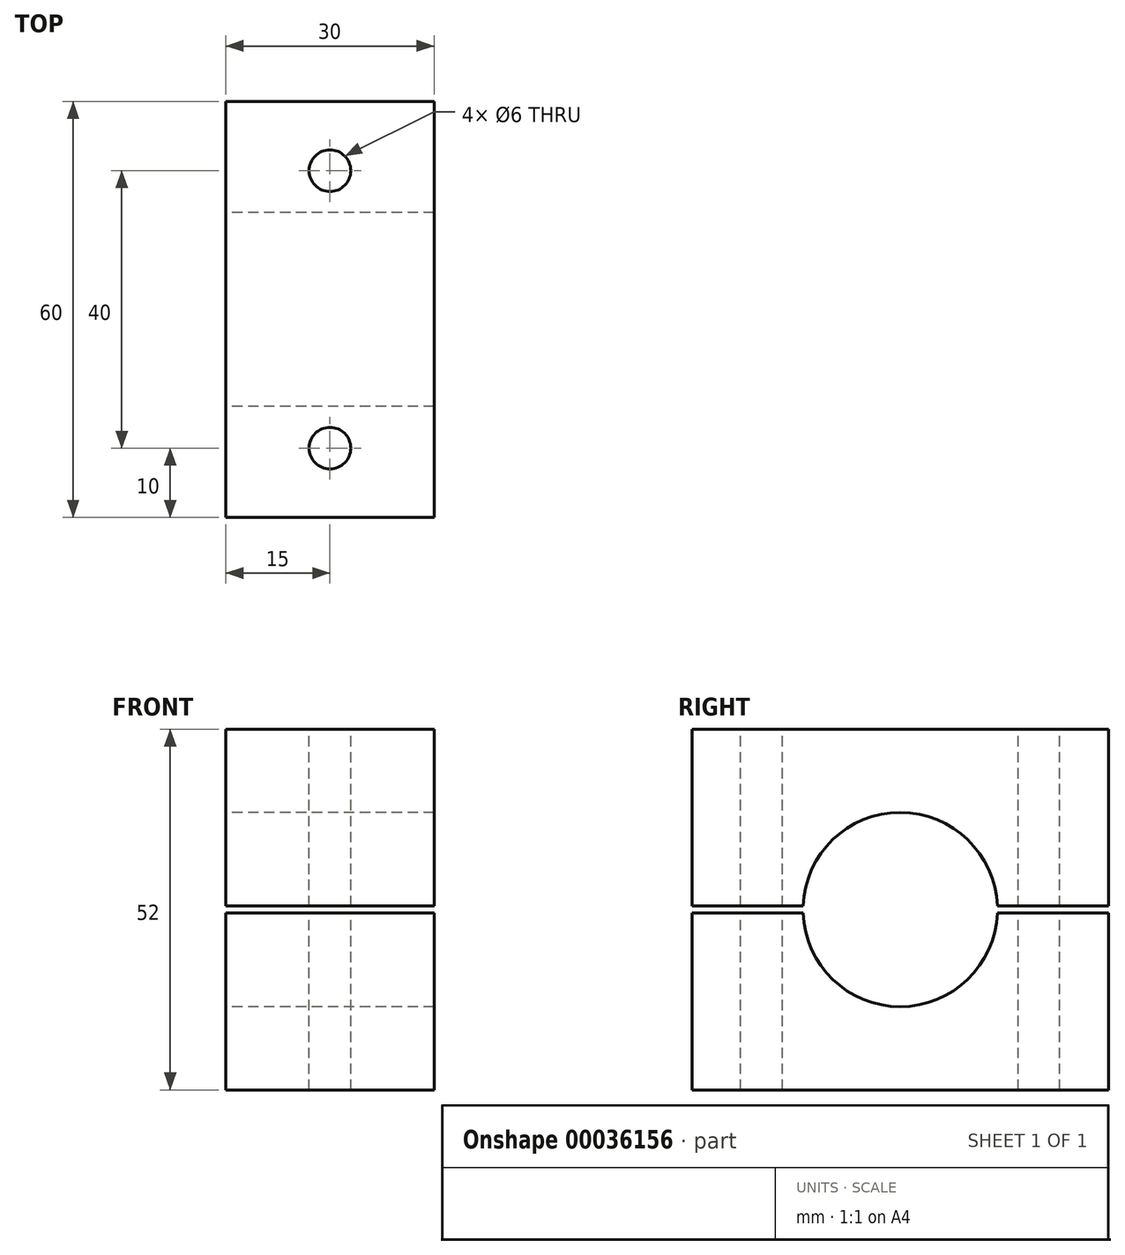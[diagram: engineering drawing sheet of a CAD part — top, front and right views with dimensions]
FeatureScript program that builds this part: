
annotation { "Feature Type Name" : "Feature", "Feature Type Description" : "" }
export const myFeature = defineFeature(function(context is Context, id is Id, definition is map)
    precondition{}
    {
        {
            var Q0;
            Q0=qCreatedBy(makeId("Right.planeOp"),FACE);
            var sketch = newSketch(context, id + "F0", { "sketchPlane" : qUnion([Q0])});
            skLineSegment(sketch, "E0.rect.bottom", {"start": v(30, -26) * mm, "end": v(-30, -26) * mm});
            skLineSegment(sketch, "E0.rect.top", {"start": v(30, 26) * mm, "end": v(-30, 26) * mm});
            skPoint(sketch, "E0.rect.middle", {"position": v(0, 0) * mm});
            skArc(sketch, "E1", {"start": v(-14, -0.5) * mm, "mid": v(0, -14) * mm, "end": v(14, -0.5) * mm});
            skLineSegment(sketch, "E2", {"start": v(-30, 26) * mm, "end": v(-30, 0.5) * mm});
            skLineSegment(sketch, "E3", {"start": v(30, -26) * mm, "end": v(30, -0.5) * mm});
            skLineSegment(sketch, "E4.0", {"start": v(-30, -0.5) * mm, "end": v(-14, -0.5) * mm});
            skLineSegment(sketch, "E5.0", {"start": v(-30, 0.5) * mm, "end": v(-14, 0.5) * mm});
            skLineSegment(sketch, "E6.trimOffspring", {"start": v(14, -0.5) * mm, "end": v(30, -0.5) * mm});
            skLineSegment(sketch, "E7.trimOffspring", {"start": v(14, 0.5) * mm, "end": v(30, 0.5) * mm});
            skLineSegment(sketch, "E8.trimOffspring", {"start": v(-30, -0.5) * mm, "end": v(-30, -26) * mm});
            skArc(sketch, "E9.trimOffspring", {"start": v(14, 0.5) * mm, "mid": v(0, 14) * mm, "end": v(-14, 0.5) * mm});
            skLineSegment(sketch, "E10.trimOffspring", {"start": v(30, 0.5) * mm, "end": v(30, 26) * mm});
            skSolve(sketch);
        }
        {
            var Q0;
            Q0 = qSketchRegion(id + "F0", true);
            extrude(context, id + "F1", {"entities" : qUnion([Q0]), "depth" : 30 * mm});
        }
        {
            var Q0;
            Q0=makeQuery(id+"F1.opExtrude","SWEPT_FACE",FACE,{"disambiguationData":[OSD([sQuery(id+"F0.wireOp",EDGE,"E0.rect.top")])]});
            var sketch = newSketch(context, id + "F2", { "sketchPlane" : qUnion([Q0])});
            skCircle(sketch, "E11", {"center": v(15, 20) * mm, "radius": 3 * mm});
            skCircle(sketch, "E12", {"center": v(15, -20) * mm, "radius": 3 * mm});
            skSolve(sketch);
        }
        {
            var Q0;
            Q0 = qSketchRegion(id + "F2", true);
            extrude(context, id + "F3", {"entities" : qUnion([Q0]), "operationType" : NewBodyOperationType.REMOVE, "oppositeDirection" : true, "depth" : 52 * mm});
        }
    });
